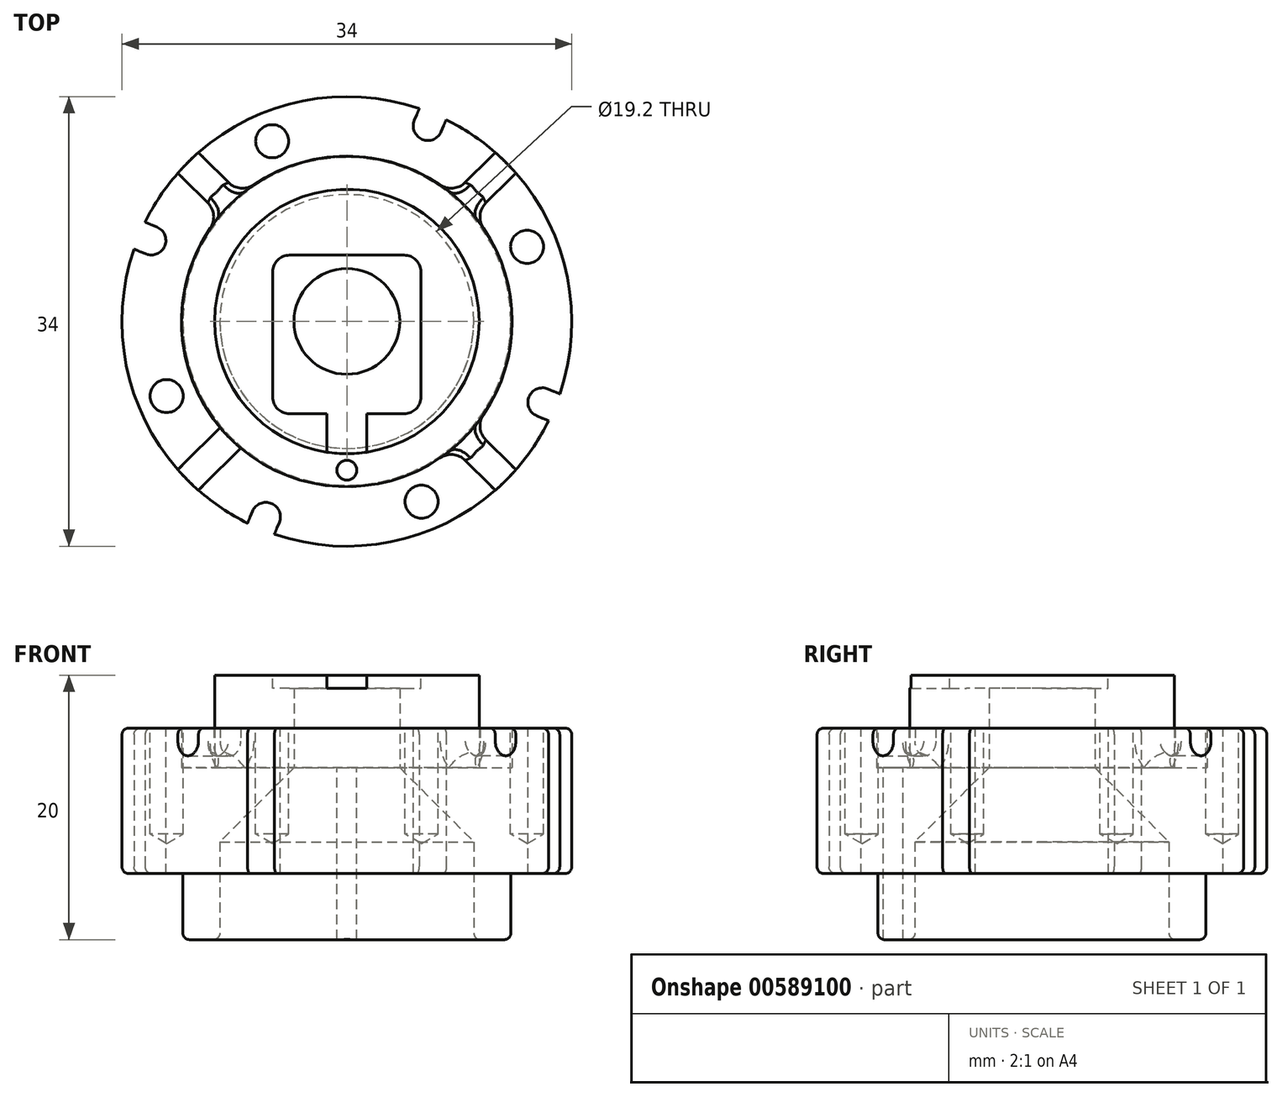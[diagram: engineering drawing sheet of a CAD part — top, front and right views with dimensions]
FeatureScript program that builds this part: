
annotation { "Feature Type Name" : "Feature", "Feature Type Description" : "" }
export const myFeature = defineFeature(function(context is Context, id is Id, definition is map)
    precondition{}
    {
        {
            var Q0;
            Q0=qCreatedBy(makeId("Front.planeOp"),FACE);
            var sketch = newSketch(context, id + "F0", { "sketchPlane" : qUnion([Q0])});
            skLineSegment(sketch, "E0", {"start": v(-9.6, -7) * mm, "end": v(-9.6, 0.4) * mm});
            skLineSegment(sketch, "E1", {"start": v(-9.6, 0.4) * mm, "end": v(-4, 6) * mm});
            skLineSegment(sketch, "E2", {"start": v(-4, 6) * mm, "end": v(-4, 13) * mm});
            skLineSegment(sketch, "E3", {"start": v(-4, 13) * mm, "end": v(-10, 13) * mm});
            skLineSegment(sketch, "E4", {"start": v(-17, 9) * mm, "end": v(-17, -2) * mm});
            skLineSegment(sketch, "E5", {"start": v(-17, -2) * mm, "end": v(-12.4, -2) * mm});
            skLineSegment(sketch, "E6", {"start": v(-12.4, -2) * mm, "end": v(-12.4, -7) * mm});
            skLineSegment(sketch, "E7", {"start": v(-12.4, -7) * mm, "end": v(-9.6, -7) * mm});
            skLineSegment(sketch, "E8", {"start": v(0, 0) * mm, "end": v(0, 16.77) * mm, "construction": true});
            skLineSegment(sketch, "E9", {"start": v(-12.5, 9) * mm, "end": v(-12.5, 6) * mm});
            skLineSegment(sketch, "E10", {"start": v(-12.5, 6) * mm, "end": v(-10, 6) * mm});
            skLineSegment(sketch, "E11", {"start": v(-10, 6) * mm, "end": v(-10, 13) * mm});
            skLineSegment(sketch, "E12.trimOffspring", {"start": v(-12.5, 9) * mm, "end": v(-17, 9) * mm});
            skSolve(sketch);
        }
        {
            var Q0;
            Q0 = qSketchRegion(id + "F0", true);
            var Q1;
            Q1=sQuery(id+"F0.wireOp",EDGE,"E8");
            revolve(context, id + "F1", {"entities" : qUnion([Q0]), "axis" : qUnion([Q1]), "revolveType" : RevolveType.FULL});
        }
        {
            var Q0;
            Q0=makeQuery(id+"F1.opRevolve","SWEPT_FACE",FACE,{"disambiguationData":[OSD([sQuery(id+"F0.wireOp",EDGE,"E3")])]});
            var sketch = newSketch(context, id + "F2", { "sketchPlane" : qUnion([Q0])});
            skLineSegment(sketch, "E13.bottom", {"start": v(-4.33, 5) * mm, "end": v(4.33, 5) * mm});
            skLineSegment(sketch, "E13.top", {"start": v(-4.33, -7) * mm, "end": v(-1.5, -7) * mm});
            skLineSegment(sketch, "E13.left", {"start": v(-5.6, 3.74) * mm, "end": v(-5.6, -5.72) * mm});
            skLineSegment(sketch, "E13.right", {"start": v(5.6, 3.74) * mm, "end": v(5.6, -5.72) * mm});
            skPoint(sketch, "E14.visualSharp", {"position": v(-5.6, 5) * mm});
            skArc(sketch, "E14.filletArc", {"start": v(-4.33, 5) * mm, "mid": v(-5.23, 4.64) * mm, "end": v(-5.6, 3.74) * mm});
            skPoint(sketch, "E15.visualSharp", {"position": v(5.6, 5) * mm});
            skArc(sketch, "E15.filletArc", {"start": v(5.6, 3.74) * mm, "mid": v(5.23, 4.64) * mm, "end": v(4.33, 5) * mm});
            skPoint(sketch, "E16.visualSharp", {"position": v(5.6, -7) * mm});
            skArc(sketch, "E16.filletArc", {"start": v(4.33, -7) * mm, "mid": v(5.23, -6.62) * mm, "end": v(5.6, -5.72) * mm});
            skPoint(sketch, "E17.visualSharp", {"position": v(-5.6, -7) * mm});
            skArc(sketch, "E17.filletArc", {"start": v(-5.6, -5.72) * mm, "mid": v(-5.23, -6.62) * mm, "end": v(-4.33, -6.99) * mm});
            skLineSegment(sketch, "E18", {"start": v(-1.5, -7) * mm, "end": v(-1.5, -11) * mm});
            skLineSegment(sketch, "E19", {"start": v(1.5, -11) * mm, "end": v(1.5, -7) * mm});
            skLineSegment(sketch, "E20.trimOffspring", {"start": v(1.5, -7) * mm, "end": v(4.33, -7) * mm});
            skLineSegment(sketch, "E21", {"start": v(-1.5, -11) * mm, "end": v(1.5, -11) * mm});
            skSolve(sketch);
        }
        {
            var Q0;
            Q0 = qSketchRegion(id + "F2", true);
            extrude(context, id + "F3", {"entities" : qUnion([Q0]), "operationType" : NewBodyOperationType.REMOVE, "oppositeDirection" : true, "depth" : 1 * mm, "offsetDistance" : 25 * mm});
        }
        {
            var Q0;
            Q0=makeQuery(id+"F1.opRevolve","SWEPT_FACE",FACE,{"disambiguationData":[OSD([sQuery(id+"F0.wireOp",EDGE,"E12.trimOffspring")])]});
            var sketch = newSketch(context, id + "F4", { "sketchPlane" : qUnion([Q0])});
            skLineSegment(sketch, "E22", {"start": v(-14.78, 6.12) * mm, "end": v(14.78, -6.12) * mm, "construction": true});
            skLineSegment(sketch, "E23.trimOffspring", {"start": v(6.12, 14.78) * mm, "end": v(-6.12, -14.78) * mm, "construction": true});
            skCircle(sketch, "E24", {"center": v(0, 0) * mm, "radius": 16 * mm, "construction": true});
            skLineSegment(sketch, "E25.bottom", {"start": v(6.12, 14.78) * mm, "end": v(7.14, 14.36) * mm, "construction": true});
            skLineSegment(sketch, "E25.top", {"start": v(5.57, 16.31) * mm, "end": v(7.6, 15.47) * mm});
            skLineSegment(sketch, "E25.right", {"start": v(7.14, 14.36) * mm, "end": v(7.6, 15.47) * mm});
            skLineSegment(sketch, "E26", {"start": v(6.12, 14.78) * mm, "end": v(5.1, 15.2) * mm, "construction": true});
            skLineSegment(sketch, "E27", {"start": v(5.1, 15.2) * mm, "end": v(5.57, 16.31) * mm});
            skArc(sketch, "E28", {"start": v(7.14, 14.36) * mm, "mid": v(5.7, 13.77) * mm, "end": v(5.1, 15.2) * mm});
            skLineSegment(sketch, "E29.1.0", {"start": v(-14.78, 6.12) * mm, "end": v(-14.36, 7.14) * mm, "construction": true});
            skLineSegment(sketch, "E29.1.1", {"start": v(-16.31, 5.57) * mm, "end": v(-15.47, 7.6) * mm});
            skLineSegment(sketch, "E29.1.2", {"start": v(-14.36, 7.14) * mm, "end": v(-15.47, 7.6) * mm});
            skLineSegment(sketch, "E29.1.3", {"start": v(-14.78, 6.12) * mm, "end": v(-15.2, 5.1) * mm, "construction": true});
            skLineSegment(sketch, "E29.1.4", {"start": v(-15.2, 5.1) * mm, "end": v(-16.31, 5.57) * mm});
            skArc(sketch, "E29.1.5", {"start": v(-14.36, 7.14) * mm, "mid": v(-13.77, 5.7) * mm, "end": v(-15.2, 5.1) * mm});
            skLineSegment(sketch, "E29.2.0", {"start": v(-6.12, -14.78) * mm, "end": v(-7.14, -14.36) * mm, "construction": true});
            skLineSegment(sketch, "E29.2.1", {"start": v(-5.57, -16.31) * mm, "end": v(-7.6, -15.47) * mm});
            skLineSegment(sketch, "E29.2.2", {"start": v(-7.14, -14.36) * mm, "end": v(-7.6, -15.47) * mm});
            skLineSegment(sketch, "E29.2.3", {"start": v(-6.12, -14.78) * mm, "end": v(-5.1, -15.2) * mm, "construction": true});
            skLineSegment(sketch, "E29.2.4", {"start": v(-5.1, -15.2) * mm, "end": v(-5.57, -16.31) * mm});
            skArc(sketch, "E29.2.5", {"start": v(-7.14, -14.36) * mm, "mid": v(-5.7, -13.77) * mm, "end": v(-5.1, -15.2) * mm});
            skLineSegment(sketch, "E29.3.0", {"start": v(14.78, -6.12) * mm, "end": v(14.36, -7.14) * mm, "construction": true});
            skLineSegment(sketch, "E29.3.1", {"start": v(16.31, -5.57) * mm, "end": v(15.47, -7.6) * mm});
            skLineSegment(sketch, "E29.3.2", {"start": v(14.36, -7.14) * mm, "end": v(15.47, -7.6) * mm});
            skLineSegment(sketch, "E29.3.3", {"start": v(14.78, -6.12) * mm, "end": v(15.2, -5.1) * mm, "construction": true});
            skLineSegment(sketch, "E29.3.4", {"start": v(15.2, -5.1) * mm, "end": v(16.31, -5.57) * mm});
            skArc(sketch, "E29.3.5", {"start": v(14.36, -7.14) * mm, "mid": v(13.77, -5.7) * mm, "end": v(15.2, -5.1) * mm});
            skSolve(sketch);
        }
        {
            var Q0;
            Q0 = qSketchRegion(id + "F4", true);
            extrude(context, id + "F5", {"entities" : qUnion([Q0]), "operationType" : NewBodyOperationType.REMOVE, "oppositeDirection" : true, "depth" : 25 * mm, "offsetDistance" : 25 * mm});
        }
        {
            var Q0;
            Q0=qCreatedBy(makeId("Front.planeOp"),FACE);
            var Q1;
            Q1=qCreatedBy(makeId("Right.planeOp"),FACE);
            cPlane(context, id + "F6", {"entities" : qUnion([Q0, Q1]), "cplaneType" : CPlaneType.MID_PLANE, "offset" : 25 * mm, "width" : 150 * mm, "height" : 150 * mm});
        }
        {
            var Q0;
            Q0=qCreatedBy(makeId("Right.planeOp"),FACE);
            var Q1;
            Q1=qCreatedBy(makeId("Front.planeOp"),FACE);
            cPlane(context, id + "F7", {"entities" : qUnion([Q0, Q1]), "cplaneType" : CPlaneType.MID_PLANE, "offset" : 25 * mm, "flipAlignment" : true, "width" : 150 * mm, "height" : 150 * mm});
        }
        {
            var Q0;
            Q0=qCreatedBy(id+"F6.planeOp",FACE);
            cPlane(context, id + "F8", {"entities" : qUnion([Q0]), "cplaneType" : CPlaneType.OFFSET, "offset" : 12 * mm, "width" : 150 * mm, "height" : 150 * mm});
        }
        {
            var Q0;
            Q0=qCreatedBy(id+"F8.planeOp",FACE);
            var sketch = newSketch(context, id + "F9", { "sketchPlane" : qUnion([Q0])});
            skArc(sketch, "E30", {"start": v(-1.1, 8) * mm, "mid": v(0, 6.9) * mm, "end": v(1.1, 8) * mm});
            skLineSegment(sketch, "E31", {"start": v(-1.1, 8) * mm, "end": v(-1.1, 10) * mm});
            skLineSegment(sketch, "E32", {"start": v(1.1, 8) * mm, "end": v(1.1, 10) * mm});
            skLineSegment(sketch, "E33", {"start": v(1.1, 10) * mm, "end": v(-1.1, 10) * mm});
            skSolve(sketch);
        }
        {
            var Q0;
            Q0 = qSketchRegion(id + "F9", true);
            extrude(context, id + "F10", {"entities" : qUnion([Q0]), "operationType" : NewBodyOperationType.REMOVE, "depth" : 5 * mm, "offsetDistance" : 25 * mm});
        }
        {
            var Q0;
            Q0=qCreatedBy(id+"F6.planeOp",FACE);
            cPlane(context, id + "F11", {"entities" : qUnion([Q0]), "cplaneType" : CPlaneType.OFFSET, "offset" : 12 * mm, "oppositeDirection" : true, "width" : 150 * mm, "height" : 150 * mm});
        }
        {
            var Q0;
            Q0=qCreatedBy(id+"F11.planeOp",FACE);
            var sketch = newSketch(context, id + "F12", { "sketchPlane" : qUnion([Q0])});
            skLineSegment(sketch, "E34.bottom", {"start": v(1.1, 10) * mm, "end": v(-1.1, 10) * mm});
            skLineSegment(sketch, "E34.top", {"start": v(1.1, 8) * mm, "end": v(-1.1, 8) * mm, "construction": true});
            skLineSegment(sketch, "E34.left", {"start": v(1.1, 10) * mm, "end": v(1.1, 8) * mm});
            skLineSegment(sketch, "E34.right", {"start": v(-1.1, 10) * mm, "end": v(-1.1, 8) * mm});
            skArc(sketch, "E35", {"start": v(-1.1, 8) * mm, "mid": v(0, 6.9) * mm, "end": v(1.1, 8) * mm});
            skSolve(sketch);
        }
        {
            var Q0;
            Q0 = qSketchRegion(id + "F12", true);
            extrude(context, id + "F13", {"entities" : qUnion([Q0]), "operationType" : NewBodyOperationType.REMOVE, "oppositeDirection" : true, "depth" : 5 * mm, "offsetDistance" : 25 * mm});
        }
        {
            var Q0;
            Q0=qCreatedBy(id+"F7.planeOp",FACE);
            cPlane(context, id + "F14", {"entities" : qUnion([Q0]), "cplaneType" : CPlaneType.OFFSET, "offset" : 12 * mm, "width" : 150 * mm, "height" : 150 * mm});
        }
        {
            var Q0;
            Q0=qCreatedBy(id+"F14.planeOp",FACE);
            var sketch = newSketch(context, id + "F15", { "sketchPlane" : qUnion([Q0])});
            skLineSegment(sketch, "E36.bottom", {"start": v(-1.1, 10) * mm, "end": v(1.1, 10) * mm});
            skLineSegment(sketch, "E36.top", {"start": v(-1.1, 8) * mm, "end": v(1.1, 8) * mm, "construction": true});
            skLineSegment(sketch, "E36.left", {"start": v(-1.1, 10) * mm, "end": v(-1.1, 8) * mm});
            skLineSegment(sketch, "E36.right", {"start": v(1.1, 10) * mm, "end": v(1.1, 8) * mm});
            skArc(sketch, "E37", {"start": v(1.1, 8) * mm, "mid": v(0, 6.9) * mm, "end": v(-1.1, 8) * mm});
            skSolve(sketch);
        }
        {
            var Q0;
            Q0 = qSketchRegion(id + "F15", true);
            extrude(context, id + "F16", {"entities" : qUnion([Q0]), "operationType" : NewBodyOperationType.REMOVE, "depth" : 5 * mm, "offsetDistance" : 25 * mm});
        }
        {
            var Q0;
            Q0=qCreatedBy(id+"F7.planeOp",FACE);
            cPlane(context, id + "F17", {"entities" : qUnion([Q0]), "cplaneType" : CPlaneType.OFFSET, "offset" : 12 * mm, "oppositeDirection" : true, "width" : 150 * mm, "height" : 150 * mm});
        }
        {
            var Q0;
            Q0=qCreatedBy(id+"F17.planeOp",FACE);
            var sketch = newSketch(context, id + "F18", { "sketchPlane" : qUnion([Q0])});
            skLineSegment(sketch, "E38.bottom", {"start": v(1.1, 10) * mm, "end": v(-1.1, 10) * mm});
            skLineSegment(sketch, "E38.top", {"start": v(1.1, 8) * mm, "end": v(-1.1, 8) * mm, "construction": true});
            skLineSegment(sketch, "E38.left", {"start": v(1.1, 10) * mm, "end": v(1.1, 8) * mm});
            skLineSegment(sketch, "E38.right", {"start": v(-1.1, 10) * mm, "end": v(-1.1, 8) * mm});
            skArc(sketch, "E39", {"start": v(-1.1, 8) * mm, "mid": v(0, 6.9) * mm, "end": v(1.1, 8) * mm});
            skPoint(sketch, "E39.centerSnap0", {"position": v(0, 8) * mm});
            skSolve(sketch);
        }
        {
            var Q0;
            Q0 = qSketchRegion(id + "F18", true);
            extrude(context, id + "F19", {"entities" : qUnion([Q0]), "operationType" : NewBodyOperationType.REMOVE, "oppositeDirection" : true, "depth" : 5 * mm, "offsetDistance" : 25 * mm});
        }
        {
            var Q0;
            Q0=makeQuery(id+"F10.boolean.opBoolean","INTERSECT",EDGE,{"disambiguationData":[OD(2.0)],"derivedFrom":[makeQuery(id+"F5.boolean.opBoolean","COPY",FACE,{"derivedFrom":makeQuery(id+"F5.opExtrude","SWEPT_FACE",FACE,{"disambiguationData":[OSD([sQuery(id+"F4.wireOp",EDGE,"z5jWrSmV-QiNL-0cdw-Nr2k-EaGTKOgJtDDY")])]})}),makeQuery(id+"F10.opExtrude","SWEPT_FACE",FACE,{"disambiguationData":[OSD([sQuery(id+"F9.wireOp",EDGE,"E30")])]})]});
            var Q1;
            Q1=makeQuery(id+"F13.boolean.opBoolean","INTERSECT",EDGE,{"derivedFrom":[makeQuery(id+"F1.opRevolve","SWEPT_FACE",FACE,{"disambiguationData":[OSD([sQuery(id+"F0.wireOp",EDGE,"E9")])]}),makeQuery(id+"F13.opExtrude","SWEPT_FACE",FACE,{"disambiguationData":[OSD([sQuery(id+"F12.wireOp",EDGE,"E34.right")])]})]});
            var Q2;
            Q2=makeQuery(id+"F13.boolean.opBoolean","INTERSECT",EDGE,{"derivedFrom":[makeQuery(id+"F5.boolean.opBoolean","COPY",FACE,{"derivedFrom":makeQuery(id+"F5.opExtrude","SWEPT_FACE",FACE,{"disambiguationData":[OSD([sQuery(id+"F4.wireOp",EDGE,"E28")])]})}),makeQuery(id+"F13.opExtrude","SWEPT_FACE",FACE,{"disambiguationData":[OSD([sQuery(id+"F12.wireOp",EDGE,"E35")])]})]});
            var Q3;
            Q3=makeQuery(id+"F19.boolean.opBoolean","INTERSECT",EDGE,{"derivedFrom":[makeQuery(id+"F5.boolean.opBoolean","COPY",FACE,{"derivedFrom":makeQuery(id+"F5.opExtrude","SWEPT_FACE",FACE,{"disambiguationData":[OSD([sQuery(id+"F4.wireOp",EDGE,"E29.1.5")])]})}),makeQuery(id+"F19.opExtrude","SWEPT_FACE",FACE,{"disambiguationData":[OSD([sQuery(id+"F18.wireOp",EDGE,"E39")])]})]});
            var Q4;
            Q4=makeQuery(id+"F19.boolean.opBoolean","INTERSECT",EDGE,{"derivedFrom":[makeQuery(id+"F1.opRevolve","SWEPT_FACE",FACE,{"disambiguationData":[OSD([sQuery(id+"F0.wireOp",EDGE,"E9")])]}),makeQuery(id+"F19.opExtrude","SWEPT_FACE",FACE,{"disambiguationData":[OSD([sQuery(id+"F18.wireOp",EDGE,"E39")])]})]});
            var Q5;
            Q5=makeQuery(id+"F16.boolean.opBoolean","INTERSECT",EDGE,{"derivedFrom":[makeQuery(id+"F5.boolean.opBoolean","COPY",FACE,{"derivedFrom":makeQuery(id+"F5.opExtrude","SWEPT_FACE",FACE,{"disambiguationData":[OSD([sQuery(id+"F4.wireOp",EDGE,"E29.3.5")])]})}),makeQuery(id+"F16.opExtrude","SWEPT_FACE",FACE,{"disambiguationData":[OSD([sQuery(id+"F15.wireOp",EDGE,"E37")])]})]});
            var Q6;
            Q6=makeQuery(id+"F16.boolean.opBoolean","INTERSECT",EDGE,{"derivedFrom":[makeQuery(id+"F1.opRevolve","SWEPT_FACE",FACE,{"disambiguationData":[OSD([sQuery(id+"F0.wireOp",EDGE,"E9")])]}),makeQuery(id+"F16.opExtrude","SWEPT_FACE",FACE,{"disambiguationData":[OSD([sQuery(id+"F15.wireOp",EDGE,"E37")])]})]});
            fillet(context, id + "F20", {"entities" : qUnion([Q0, Q1, Q2, Q3, Q4, Q5, Q6]), "radius" : 1.5 * mm, "tangentPropagation" : true, "allowEdgeOverflow" : false});
        }
        {
            var Q0;
            Q0=makeQuery(id+"F1.opRevolve","SWEPT_FACE",FACE,{"disambiguationData":[OSD([sQuery(id+"F0.wireOp",EDGE,"E10")])]});
            var sketch = newSketch(context, id + "F21", { "sketchPlane" : qUnion([Q0])});
            skCircle(sketch, "E40", {"center": v(0, -11.25) * mm, "radius": 0.75 * mm});
            skSolve(sketch);
        }
        {
            var Q0;
            Q0 = qSketchRegion(id + "F21", true);
            extrude(context, id + "F22", {"entities" : qUnion([Q0]), "operationType" : NewBodyOperationType.REMOVE, "oppositeDirection" : true, "depth" : 25 * mm, "offsetDistance" : 25 * mm});
        }
        {
            var Q0;
            {var subQ2=makeQuery(id+"F5.boolean.opBoolean","COPY",FACE,{"derivedFrom":makeQuery(id+"F5.opExtrude","SWEPT_FACE",FACE,{"disambiguationData":[OSD([sQuery(id+"F4.wireOp",EDGE,"E27")])]})});Q0=makeQuery(id+"F19.boolean.opBoolean","SPLIT",FACE,{"disambiguationData":[TD([subQ2])],"derivedFrom":makeQuery(id+"F13.boolean.opBoolean","SPLIT",FACE,{"disambiguationData":[TD([subQ2])],"derivedFrom":makeQuery(id+"F1.opRevolve","SWEPT_FACE",FACE,{"disambiguationData":[OSD([sQuery(id+"F0.wireOp",EDGE,"E12.trimOffspring")])]})})});}
            var sketch = newSketch(context, id + "F23", { "sketchPlane" : qUnion([Q0])});
            skCircle(sketch, "E41", {"center": v(-5.64, 13.63) * mm, "radius": 1.02 * mm});
            skCircle(sketch, "E42.1.0", {"center": v(-13.63, -5.64) * mm, "radius": 1.02 * mm});
            skCircle(sketch, "E42.2.0", {"center": v(5.64, -13.63) * mm, "radius": 1.02 * mm});
            skCircle(sketch, "E42.3.0", {"center": v(13.63, 5.64) * mm, "radius": 1.02 * mm});
            skPoint(sketch, "E42.center", {"position": v(0, 0) * mm});
            skLineSegment(sketch, "E43", {"start": v(-5.64, 13.63) * mm, "end": v(0, 0) * mm, "construction": true});
            skSolve(sketch);
        }
        {
            var Q0;
            Q0=sQuery(id+"F23.wireOp",VERTEX,"E41.center");
            var Q1;
            Q1=sQuery(id+"F23.wireOp",VERTEX,"E42.3.0.center");
            var Q2;
            Q2=sQuery(id+"F23.wireOp",VERTEX,"E42.2.0.center");
            var Q3;
            Q3=sQuery(id+"F23.wireOp",VERTEX,"E42.1.0.center");
            var Q4;
            Q4=makeQuery(id+"F1.opRevolve","SWEPT_BODY",BODY,{"disambiguationData":[OSD([sQuery(id+"F0.wireOp",EDGE,"E0"),sQuery(id+"F0.wireOp",EDGE,"E1"),sQuery(id+"F0.wireOp",EDGE,"E2"),sQuery(id+"F0.wireOp",EDGE,"E3"),sQuery(id+"F0.wireOp",EDGE,"E4"),sQuery(id+"F0.wireOp",EDGE,"E5"),sQuery(id+"F0.wireOp",EDGE,"E6"),sQuery(id+"F0.wireOp",EDGE,"E7"),sQuery(id+"F0.wireOp",EDGE,"E9"),sQuery(id+"F0.wireOp",EDGE,"E10"),sQuery(id+"F0.wireOp",EDGE,"E11"),sQuery(id+"F0.wireOp",EDGE,"E12.trimOffspring")])]});
            hole(context, id + "F24", {"style" : HoleStyle.SIMPLE, "endStyle" : HoleEndStyle.BLIND, "standardTappedOrClearance" : lookupTablePath({ "standard" : "ISO", "engagement" : "75%", "pitch" : "0.5 mm", "size" : "M3", "type" : "Tapped" }), "standardBlindInLast" : lookupTablePath({ "standard" : "ISO", "engagement" : "75%", "pitch" : "0.5 mm", "size" : "M3", "type" : "Tapped" }), "holeDiameter" : 2.5 * mm, "majorDiameter" : 3 * mm, "showTappedDepth" : true, "holeDepth" : 8 * mm, "isTappedThrough" : true, "tappedDepth" : 6.5 * mm, "tapClearance" : 3, "locations" : qUnion([Q0, Q1, Q2, Q3]), "scope" : qUnion([Q4])});
        }
        {
            var Q0;
            Q0=makeQuery(id+"F1.opRevolve","SWEPT_EDGE",EDGE,{"disambiguationData":[OSD([sQuery(id+"F0.wireOp",EDGE,"E0"),sQuery(id+"F0.wireOp",EDGE,"E7")])]});
            var Q1;
            Q1=makeQuery(id+"F1.opRevolve","SWEPT_EDGE",EDGE,{"disambiguationData":[OSD([sQuery(id+"F0.wireOp",EDGE,"E6"),sQuery(id+"F0.wireOp",EDGE,"E7")])]});
            var Q2;
            {var subQ0=sQuery(id+"F0.wireOp",EDGE,"E4");var subQ1=sQuery(id+"F0.wireOp",EDGE,"E5");Q2=makeQuery(id+"F5.boolean.opBoolean","SPLIT",EDGE,{"disambiguationData":[TD([makeQuery(id+"F5.opExtrude","SWEPT_FACE",FACE,{"disambiguationData":[OSD([sQuery(id+"F4.wireOp",EDGE,"E25.right")])]})])],"derivedFrom":makeQuery(id+"F1.opRevolve","SWEPT_EDGE",EDGE,{"disambiguationData":[OSD([subQ0,subQ1])]})});}
            var Q3;
            {var subQ0=sQuery(id+"F0.wireOp",EDGE,"E4");var subQ1=sQuery(id+"F0.wireOp",EDGE,"E5");Q3=makeQuery(id+"F5.boolean.opBoolean","SPLIT",EDGE,{"disambiguationData":[TD([makeQuery(id+"F5.opExtrude","SWEPT_FACE",FACE,{"disambiguationData":[OSD([sQuery(id+"F4.wireOp",EDGE,"E27")])]})])],"derivedFrom":makeQuery(id+"F1.opRevolve","SWEPT_EDGE",EDGE,{"disambiguationData":[OSD([subQ0,subQ1])]})});}
            var Q4;
            {var subQ0=sQuery(id+"F0.wireOp",EDGE,"E4");var subQ1=sQuery(id+"F0.wireOp",EDGE,"E5");Q4=makeQuery(id+"F5.boolean.opBoolean","SPLIT",EDGE,{"disambiguationData":[TD([makeQuery(id+"F5.opExtrude","SWEPT_FACE",FACE,{"disambiguationData":[OSD([sQuery(id+"F4.wireOp",EDGE,"E29.1.4")])]})])],"derivedFrom":makeQuery(id+"F1.opRevolve","SWEPT_EDGE",EDGE,{"disambiguationData":[OSD([subQ0,subQ1])]})});}
            var Q5;
            {var subQ0=sQuery(id+"F0.wireOp",EDGE,"E4");var subQ1=sQuery(id+"F0.wireOp",EDGE,"E5");Q5=makeQuery(id+"F5.boolean.opBoolean","SPLIT",EDGE,{"disambiguationData":[TD([makeQuery(id+"F5.opExtrude","SWEPT_FACE",FACE,{"disambiguationData":[OSD([sQuery(id+"F4.wireOp",EDGE,"E29.2.4")])]})])],"derivedFrom":makeQuery(id+"F1.opRevolve","SWEPT_EDGE",EDGE,{"disambiguationData":[OSD([subQ0,subQ1])]})});}
            var Q6;
            {var subQ0=sQuery(id+"F0.wireOp",EDGE,"E4");var subQ1=sQuery(id+"F0.wireOp",EDGE,"E12.trimOffspring");Q6=makeQuery(id+"F5.boolean.opBoolean","SPLIT",EDGE,{"disambiguationData":[TD([makeQuery(id+"F5.opExtrude","SWEPT_FACE",FACE,{"disambiguationData":[OSD([sQuery(id+"F4.wireOp",EDGE,"E25.right")])]})])],"derivedFrom":makeQuery(id+"F1.opRevolve","SWEPT_EDGE",EDGE,{"disambiguationData":[OSD([subQ0,subQ1])]})});}
            var Q7;
            {var subQ0=sQuery(id+"F0.wireOp",EDGE,"E4");var subQ1=sQuery(id+"F0.wireOp",EDGE,"E12.trimOffspring");Q7=makeQuery(id+"F5.boolean.opBoolean","SPLIT",EDGE,{"disambiguationData":[TD([makeQuery(id+"F5.opExtrude","SWEPT_FACE",FACE,{"disambiguationData":[OSD([sQuery(id+"F4.wireOp",EDGE,"E27")])]})])],"derivedFrom":makeQuery(id+"F1.opRevolve","SWEPT_EDGE",EDGE,{"disambiguationData":[OSD([subQ0,subQ1])]})});}
            var Q8;
            {var subQ0=sQuery(id+"F0.wireOp",EDGE,"E4");var subQ1=sQuery(id+"F0.wireOp",EDGE,"E12.trimOffspring");Q8=makeQuery(id+"F5.boolean.opBoolean","SPLIT",EDGE,{"disambiguationData":[TD([makeQuery(id+"F5.opExtrude","SWEPT_FACE",FACE,{"disambiguationData":[OSD([sQuery(id+"F4.wireOp",EDGE,"E29.2.4")])]})])],"derivedFrom":makeQuery(id+"F1.opRevolve","SWEPT_EDGE",EDGE,{"disambiguationData":[OSD([subQ0,subQ1])]})});}
            var Q9;
            {var subQ0=sQuery(id+"F0.wireOp",EDGE,"E4");var subQ1=sQuery(id+"F0.wireOp",EDGE,"E12.trimOffspring");Q9=makeQuery(id+"F5.boolean.opBoolean","SPLIT",EDGE,{"disambiguationData":[TD([makeQuery(id+"F5.opExtrude","SWEPT_FACE",FACE,{"disambiguationData":[OSD([sQuery(id+"F4.wireOp",EDGE,"E29.1.4")])]})])],"derivedFrom":makeQuery(id+"F1.opRevolve","SWEPT_EDGE",EDGE,{"disambiguationData":[OSD([subQ0,subQ1])]})});}
            fillet(context, id + "F25", {"entities" : qUnion([Q0, Q1, Q2, Q3, Q4, Q5, Q6, Q7, Q8, Q9]), "radius" : .5 * mm, "tangentPropagation" : true, "allowEdgeOverflow" : false});
        }
    });
